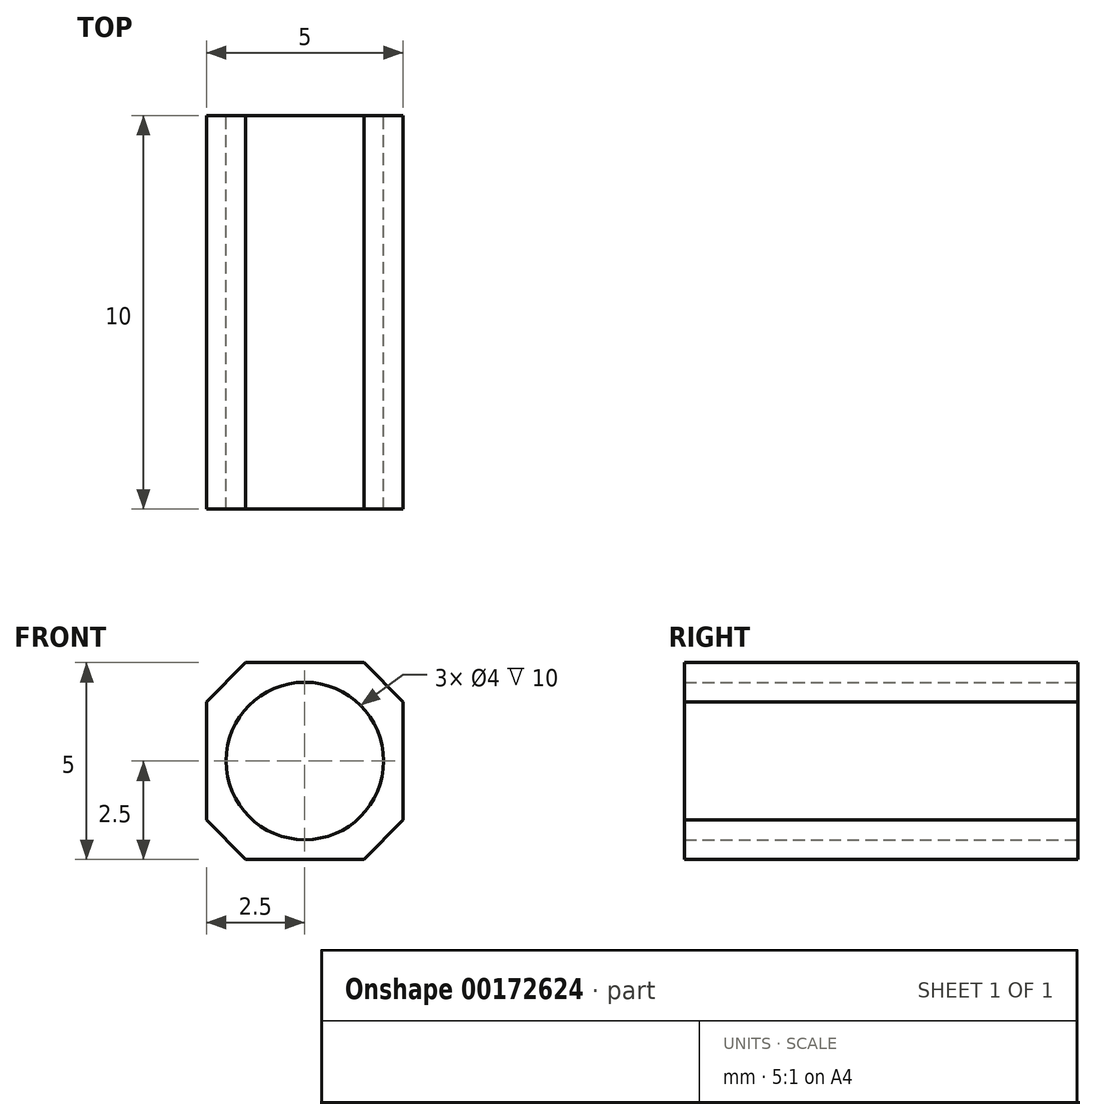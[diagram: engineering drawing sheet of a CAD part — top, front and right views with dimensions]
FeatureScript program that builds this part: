
annotation { "Feature Type Name" : "Feature", "Feature Type Description" : "" }
export const myFeature = defineFeature(function(context is Context, id is Id, definition is map)
    precondition{}
    {
        {
            var Q0;
            Q0=qCreatedBy(makeId("Top.planeOp"),FACE);
            var sketch = newSketch(context, id + "F0", { "sketchPlane" : qUnion([Q0])});
            skLineSegment(sketch, "E0.bottom", {"start": v(-1.5, 2.5) * mm, "end": v(1.5, 2.5) * mm});
            skLineSegment(sketch, "E0.top", {"start": v(-1.5, -2.5) * mm, "end": v(1.5, -2.5) * mm});
            skLineSegment(sketch, "E0.left", {"start": v(-2.5, 1.5) * mm, "end": v(-2.5, -1.5) * mm});
            skLineSegment(sketch, "E0.right", {"start": v(2.5, 1.5) * mm, "end": v(2.5, -1.5) * mm});
            skPoint(sketch, "E0.middle", {"position": v(0, 0) * mm});
            skPoint(sketch, "E1", {"position": v(0, 2.5) * mm});
            skPoint(sketch, "E2", {"position": v(2.5, 0) * mm});
            skPoint(sketch, "E3", {"position": v(0, -2.5) * mm});
            skPoint(sketch, "E4", {"position": v(-2.5, 0) * mm});
            skPoint(sketch, "E5", {"position": v(-2.5, 1.5) * mm});
            skPoint(sketch, "E6", {"position": v(-1.5, 2.5) * mm});
            skPoint(sketch, "E7", {"position": v(2.5, 1.5) * mm});
            skPoint(sketch, "E8", {"position": v(1.5, -2.5) * mm});
            skPoint(sketch, "E9.MirrorP", {"position": v(-2.5, -1.5) * mm});
            skPoint(sketch, "E10.MirrorP", {"position": v(2.5, -1.5) * mm});
            skPoint(sketch, "E11.MirrorP", {"position": v(1.5, 2.5) * mm});
            skPoint(sketch, "E12.MirrorP", {"position": v(-1.5, -2.5) * mm});
            skLineSegment(sketch, "E13", {"start": v(-2.5, 1.5) * mm, "end": v(-1.5, 2.5) * mm});
            skLineSegment(sketch, "E14", {"start": v(1.5, 2.5) * mm, "end": v(2.5, 1.5) * mm});
            skLineSegment(sketch, "E15", {"start": v(2.5, -1.5) * mm, "end": v(1.5, -2.5) * mm});
            skLineSegment(sketch, "E16", {"start": v(-2.5, -1.5) * mm, "end": v(-1.5, -2.5) * mm});
            skCircle(sketch, "E17", {"center": v(0, 0) * mm, "radius": 2 * mm});
            skSolve(sketch);
        }
        {
            var Q0;
            Q0=makeQuery(id+"F0.imprint","IMPRINT",FACE,{"disambiguationData":[TD([[makeQuery(id+"F0.imprint","IMPRINT",EDGE,{"derivedFrom":sQuery(id+"F0.wireOp",EDGE,"E0.bottom")}),-1.0]])]});
            extrude(context, id + "F1", {"entities" : qUnion([Q0]), "depth" : 10 * mm});
        }
        {
            var Q0;
            Q0=makeQuery(id+"F1.opExtrude","SWEPT_BODY",BODY,{"disambiguationData":[OSD([sQuery(id+"F0.wireOp",EDGE,"E0.bottom"),sQuery(id+"F0.wireOp",EDGE,"E0.top"),sQuery(id+"F0.wireOp",EDGE,"E0.left"),sQuery(id+"F0.wireOp",EDGE,"E0.right"),sQuery(id+"F0.wireOp",EDGE,"E13"),sQuery(id+"F0.wireOp",EDGE,"E14"),sQuery(id+"F0.wireOp",EDGE,"E15"),sQuery(id+"F0.wireOp",EDGE,"E16"),sQuery(id+"F0.wireOp",EDGE,"E17")])]});
            var Q1;
            Q1=makeQuery(id+"F1.opExtrude","CAP_EDGE",EDGE,{"disambiguationData":[OSD([sQuery(id+"F0.wireOp",EDGE,"E0.top")])],"isStart":true});
            transform(context, id + "F2", {"entities" : qUnion([Q0]), "transformType" : TransformType.ROTATION, "transformAxis" : qUnion([Q1]), "angle" : 90 * degree, "makeCopy" : false});
        }
    });
